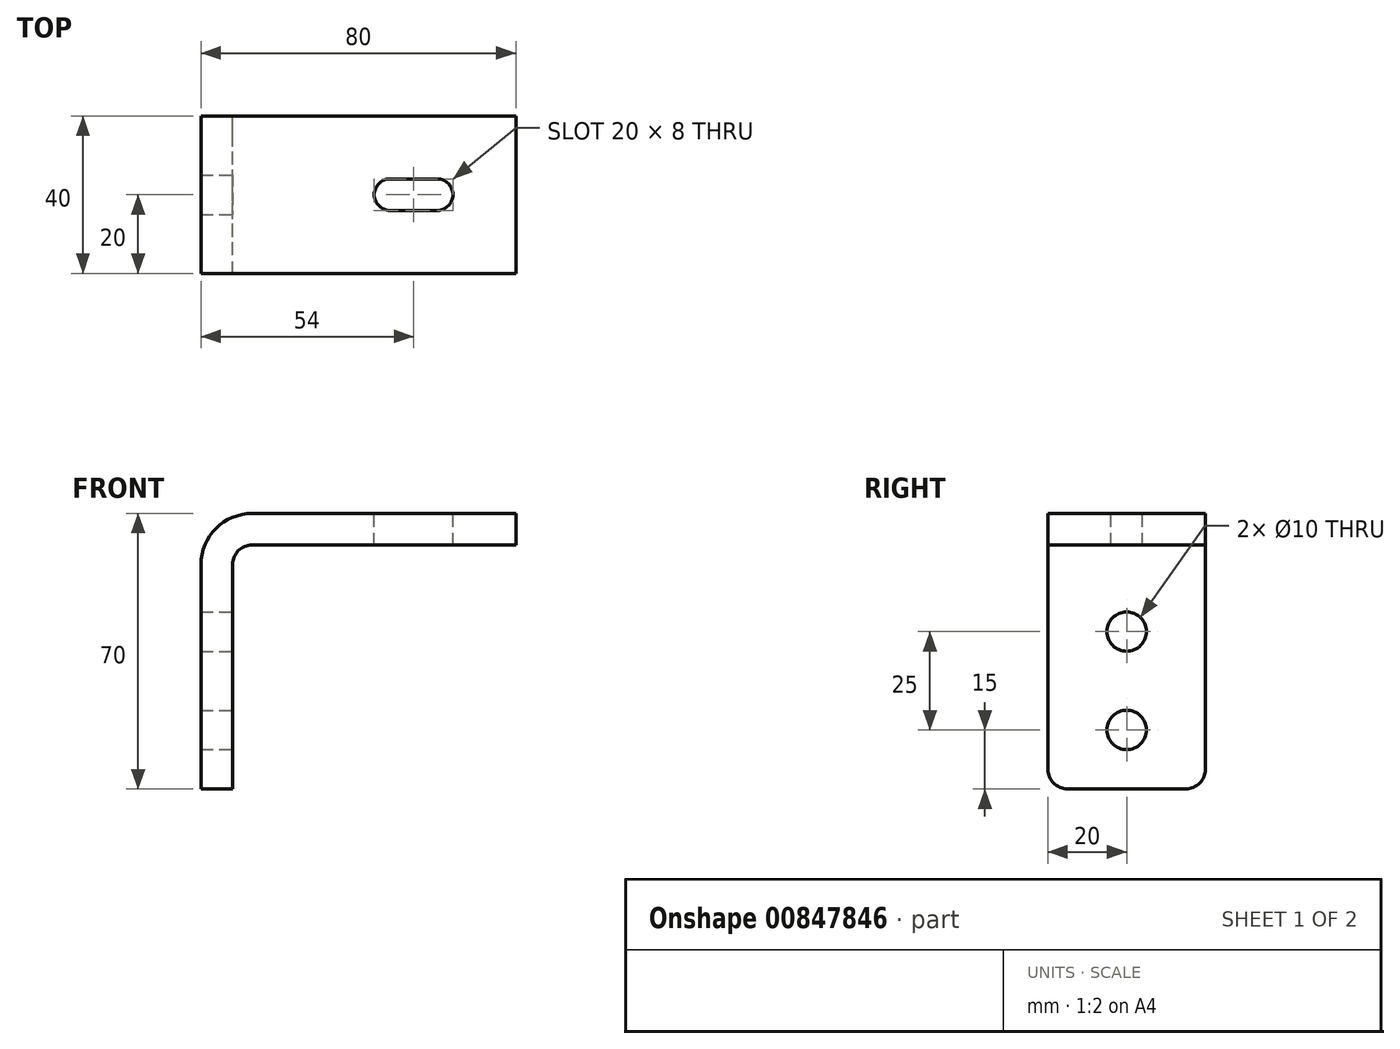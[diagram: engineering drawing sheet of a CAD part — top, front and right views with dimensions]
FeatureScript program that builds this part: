
annotation { "Feature Type Name" : "Feature", "Feature Type Description" : "" }
export const myFeature = defineFeature(function(context is Context, id is Id, definition is map)
    precondition{}
    {
        {
            var Q0;
            Q0=qCreatedBy(makeId("Front.planeOp"),FACE);
            var sketch = newSketch(context, id + "F0", { "sketchPlane" : qUnion([Q0])});
            skLineSegment(sketch, "E0.bottom", {"start": v(-32, -35) * mm, "end": v(-40, -35) * mm});
            skLineSegment(sketch, "E0.top", {"start": v(40, 35) * mm, "end": v(-27, 35) * mm});
            skLineSegment(sketch, "E0.left", {"start": v(40, 27) * mm, "end": v(40, 35) * mm});
            skLineSegment(sketch, "E0.right", {"start": v(-40, -35) * mm, "end": v(-40, 22) * mm});
            skPoint(sketch, "E0.middle", {"position": v(0, 0) * mm});
            skLineSegment(sketch, "E1", {"start": v(40, 35) * mm, "end": v(40, 27) * mm});
            skLineSegment(sketch, "E2", {"start": v(40, 27) * mm, "end": v(-27, 27) * mm});
            skLineSegment(sketch, "E3", {"start": v(-32, 22) * mm, "end": v(-32, -35) * mm});
            skPoint(sketch, "E4.orphan", {"position": v(40, -35) * mm});
            skPoint(sketch, "E5.visualSharp", {"position": v(-32, 27) * mm});
            skArc(sketch, "E5.filletArc", {"start": v(-27, 27) * mm, "mid": v(-30.54, 25.54) * mm, "end": v(-32, 22) * mm});
            skPoint(sketch, "E6.visualSharp", {"position": v(-40, 35) * mm});
            skArc(sketch, "E6.filletArc", {"start": v(-27, 35) * mm, "mid": v(-36.2, 31.2) * mm, "end": v(-40, 22) * mm});
            skSolve(sketch);
        }
        {
            var Q0;
            Q0 = qSketchRegion(id + "F0", true);
            extrude(context, id + "F1", {"entities" : qUnion([Q0]), "endBound" : BoundingType.SYMMETRIC, "depth" : 40 * mm, "offsetDistance" : 25 * mm});
        }
        {
            var Q0;
            Q0=makeQuery(id+"F1.opExtrude","CAP_EDGE",EDGE,{"disambiguationData":[OSD([sQuery(id+"F0.wireOp",EDGE,"E1")])],"isStart":false});
            var Q1;
            Q1=makeQuery(id+"F1.opExtrude","CAP_EDGE",EDGE,{"disambiguationData":[OSD([sQuery(id+"F0.wireOp",EDGE,"E1")])],"isStart":true});
            var Q2;
            Q2=makeQuery(id+"F1.opExtrude","CAP_EDGE",EDGE,{"disambiguationData":[OSD([sQuery(id+"F0.wireOp",EDGE,"E0.bottom")])],"isStart":false});
            var Q3;
            Q3=makeQuery(id+"F1.opExtrude","CAP_EDGE",EDGE,{"disambiguationData":[OSD([sQuery(id+"F0.wireOp",EDGE,"E0.bottom")])],"isStart":true});
            fillet(context, id + "F2", {"entities" : qUnion([Q0, Q1, Q2, Q3]), "radius" : 5 * mm, "tangentPropagation" : true, "allowEdgeOverflow" : false});
        }
        {
            var Q0;
            Q0=makeQuery(id+"F1.opExtrude","SWEPT_FACE",FACE,{"disambiguationData":[OSD([sQuery(id+"F0.wireOp",EDGE,"E0.top")])]});
            var sketch = newSketch(context, id + "F3", { "sketchPlane" : qUnion([Q0])});
            skLineSegment(sketch, "E7.bottom", {"start": v(20, -4) * mm, "end": v(8, -4) * mm});
            skLineSegment(sketch, "E7.top", {"start": v(20, 4) * mm, "end": v(8, 4) * mm});
            skPoint(sketch, "E7.middle", {"position": v(14, 0) * mm});
            skArc(sketch, "E8", {"start": v(20, -4) * mm, "mid": v(24, 0) * mm, "end": v(20, 4) * mm});
            skArc(sketch, "E9", {"start": v(8, 4) * mm, "mid": v(4, 0) * mm, "end": v(8, -4) * mm});
            skSolve(sketch);
        }
        {
            var Q0;
            Q0=makeQuery(id+"F3.imprint","IMPRINT",FACE,{"disambiguationData":[TD([[makeQuery(id+"F3.imprint","IMPRINT",EDGE,{"derivedFrom":sQuery(id+"F3.wireOp",EDGE,"E7.bottom")}),-1.0]])]});
            extrude(context, id + "F4", {"entities" : qUnion([Q0]), "operationType" : NewBodyOperationType.REMOVE, "endBound" : BoundingType.UP_TO_NEXT, "oppositeDirection" : true, "depth" : 25 * mm, "offsetDistance" : 25 * mm});
        }
        {
            var Q0;
            Q0=makeQuery(id+"F1.opExtrude","SWEPT_FACE",FACE,{"disambiguationData":[OSD([sQuery(id+"F0.wireOp",EDGE,"E3")])]});
            var sketch = newSketch(context, id + "F5", { "sketchPlane" : qUnion([Q0])});
            skCircle(sketch, "E10", {"center": v(0, -20) * mm, "radius": 5 * mm});
            skCircle(sketch, "E11", {"center": v(0, 5) * mm, "radius": 5 * mm});
            skSolve(sketch);
        }
        {
            var Q0;
            Q0 = qSketchRegion(id + "F5", true);
            extrude(context, id + "F6", {"entities" : qUnion([Q0]), "operationType" : NewBodyOperationType.REMOVE, "endBound" : BoundingType.UP_TO_NEXT, "oppositeDirection" : true, "depth" : 25 * mm, "offsetDistance" : 25 * mm});
        }
    });
